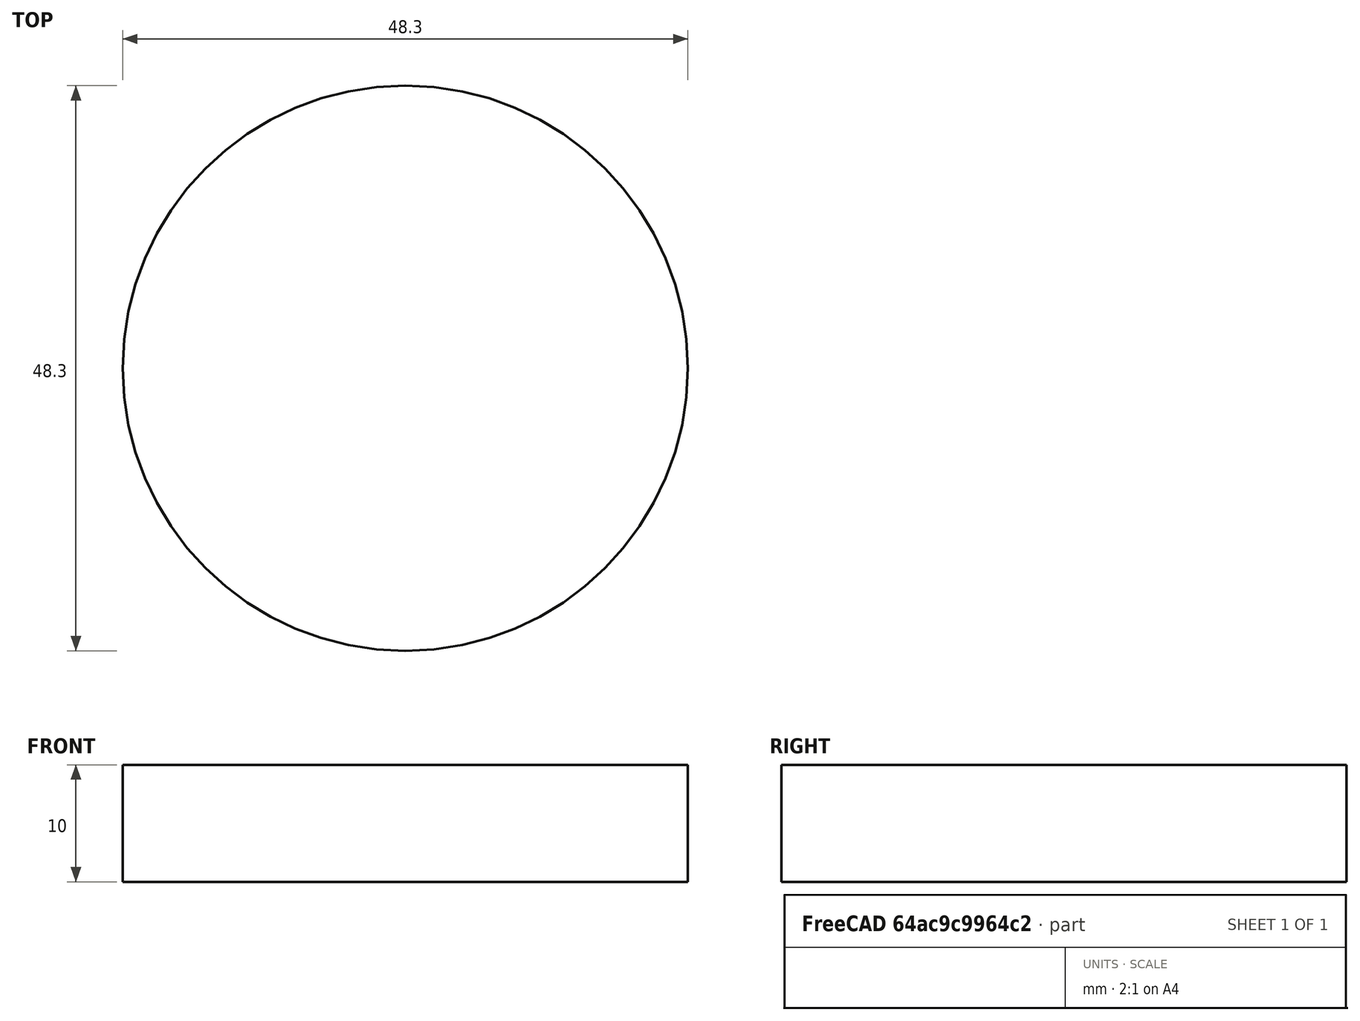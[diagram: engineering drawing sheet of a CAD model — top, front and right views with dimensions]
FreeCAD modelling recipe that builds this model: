
FCSTD DOCUMENT  (FreeCAD 0.21R33675 (Git))
Label: Tail_Hinge_Outer_Pipe_Cover
License: All rights reserved
LicenseURL: http://en.wikipedia.org/wiki/All_rights_reserved
objects: Sketcher::SketchObject×1, PartDesign::Pad×1, Spreadsheet::Sheet×1, PartDesign::Body×1
note: 4 computed .brp shape members not serialized (recipe doc carries the construction recipe); baked Part::Feature solids carry a one-line shape summary decoded from their .brp
EXTERNAL_REF file=../../../Master_of_Puppets.FCStd obj=Spreadsheet
EXTERNAL_REF file=../../../Master_of_Puppets.FCStd obj=Tail

FEATURE [Sketcher::SketchObject] Sketch
  FullyConstrained = true
  MapMode = 5
  Support = -> [XY_Plane001]
  expr: Constraints[1] = Spreadsheet.HingeOuterPipeRadius
  sketch-geometry (1):
    g0: Circle CenterX=0 CenterY=0 CenterZ=0 NormalX=0 NormalY=0 NormalZ=1 AngleXU=0 Radius=24.15
  constraints (2):
    c: Coincident(g0,g-1)
    c: Radius(g0) = 24.15
FEATURE [PartDesign::Pad] Pad
  AllowMultiFace = false
  Direction = (0,0,1)
  Length = 10
  Length2 = 100
  Profile = -> Sketch
  Type = 0
  expr: Length = Spreadsheet.FlatMetalThickness
FEATURE [Spreadsheet::Sheet] Spreadsheet
  cells = A1='Inputs; A2='HingeOuterPipeRadius; B2(HingeOuterPipeRadius)==Master_of_Puppets#Tail.HingeOuterPipeRadius; A3='FlatMetalThickness; B3(FlatMetalThickness)==Master_of_Puppets#Spreadsheet.FlatMetalThickness
FEATURE [PartDesign::Body] PadBody  label="Tail_Hinge_Outer_Pipe_Cover"
  Group = -> [Sketch,Pad]
  Openafpm_Flat = true
  Origin = -> Origin001
  Tip = -> Pad
